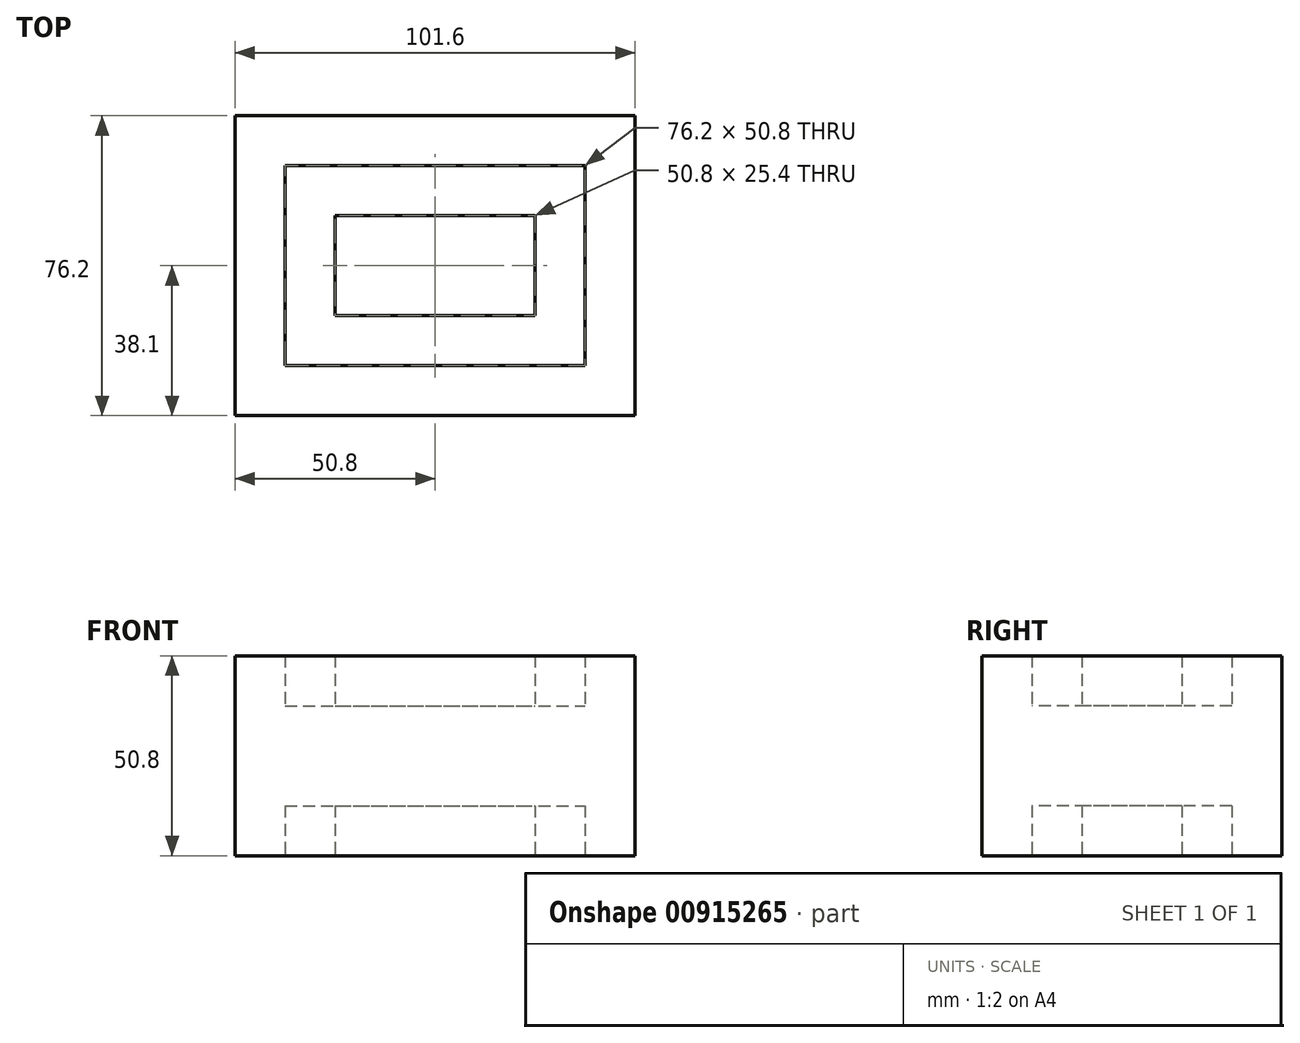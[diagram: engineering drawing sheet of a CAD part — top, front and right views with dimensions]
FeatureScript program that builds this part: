
annotation { "Feature Type Name" : "Feature", "Feature Type Description" : "" }
export const myFeature = defineFeature(function(context is Context, id is Id, definition is map)
    precondition{}
    {
        {
            var Q0;
            Q0=qCreatedBy(makeId("Top.planeOp"),FACE);
            var sketch = newSketch(context, id + "F0", { "sketchPlane" : qUnion([Q0])});
            skLineSegment(sketch, "E0.bottom", {"start": v(0, 0) * mm, "end": v(101.6, 0) * mm});
            skLineSegment(sketch, "E0.top", {"start": v(0, 76.2) * mm, "end": v(101.6, 76.2) * mm});
            skLineSegment(sketch, "E0.left", {"start": v(0, 0) * mm, "end": v(0, 76.2) * mm});
            skLineSegment(sketch, "E0.right", {"start": v(101.6, 0) * mm, "end": v(101.6, 76.2) * mm});
            skLineSegment(sketch, "E1.bottom", {"start": v(12.7, 63.5) * mm, "end": v(88.9, 63.5) * mm});
            skLineSegment(sketch, "E1.top", {"start": v(12.7, 12.7) * mm, "end": v(88.9, 12.7) * mm});
            skLineSegment(sketch, "E1.left", {"start": v(12.7, 63.5) * mm, "end": v(12.7, 12.7) * mm});
            skLineSegment(sketch, "E1.right", {"start": v(88.9, 63.5) * mm, "end": v(88.9, 12.7) * mm});
            skLineSegment(sketch, "E2.bottom", {"start": v(25.4, 50.8) * mm, "end": v(76.2, 50.8) * mm});
            skLineSegment(sketch, "E2.top", {"start": v(25.4, 25.4) * mm, "end": v(76.2, 25.4) * mm});
            skLineSegment(sketch, "E2.left", {"start": v(25.4, 50.8) * mm, "end": v(25.4, 25.4) * mm});
            skLineSegment(sketch, "E2.right", {"start": v(76.2, 50.8) * mm, "end": v(76.2, 25.4) * mm});
            skSolve(sketch);
        }
        {
            var Q0;
            Q0=makeQuery(id+"F0.imprint","IMPRINT",FACE,{"disambiguationData":[TD([[makeQuery(id+"F0.imprint","IMPRINT",EDGE,{"derivedFrom":sQuery(id+"F0.wireOp",EDGE,"E0.bottom")}),1.0]])]});
            var Q1;
            Q1=makeQuery(id+"F0.imprint","IMPRINT",FACE,{"disambiguationData":[TD([[makeQuery(id+"F0.imprint","IMPRINT",EDGE,{"derivedFrom":sQuery(id+"F0.wireOp",EDGE,"E2.bottom")}),-1.0]])]});
            extrude(context, id + "F1", {"entities" : qUnion([Q0, Q1]), "depth" : 25.4 * mm, "offsetDistance" : 25.4 * mm, "hasSecondDirection" : true, "secondDirectionOppositeDirection" : true, "secondDirectionDepth" : 25.4 * mm});
        }
        {
            var Q0;
            Q0=makeQuery(id+"F0.imprint","IMPRINT",FACE,{"disambiguationData":[TD([[makeQuery(id+"F0.imprint","IMPRINT",EDGE,{"derivedFrom":sQuery(id+"F0.wireOp",EDGE,"E1.bottom")}),-1.0]])]});
            extrude(context, id + "F2", {"entities" : qUnion([Q0]), "operationType" : NewBodyOperationType.ADD, "depth" : 12.7 * mm, "offsetDistance" : 25.4 * mm, "hasSecondDirection" : true, "secondDirectionOppositeDirection" : true, "secondDirectionDepth" : 12.7 * mm});
        }
    });
